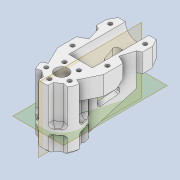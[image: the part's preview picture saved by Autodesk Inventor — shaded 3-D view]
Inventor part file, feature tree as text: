
AUTODESK INVENTOR PART (.ipt)
format: ipt  version: 2020 (Build 240168000, 168)  size: 950,784 bytes
history: native  units: mm
features: projected_geometry x29, sketch x20, extrude x17, thicken_offset x11, fillet x4, chamfer x4, other x4, plane x2, revolve x2, pattern_circular x2, mirror x2, reference x2, hole x1
ambient origin geometry x8: Origin, YZ Plane, XZ Plane, XY Plane, X Axis, Y Axis, Z Axis, Center Point
bodies: Solid1 (feature_tree)
feature tree (100):
  extrude  "Extrusion1"  Depth=12.0mm
  extrude  "Extrusion2"  Depth=18.0mm
  extrude  "Extrusion3"  Depth=20.0mm
  extrude  "Extrusion4"  Depth=60.0mm TaperAngle=0.0deg
  extrude  "Extrusion5"  Depth=45.0mm TaperAngle=0.0deg
  plane  "Work Plane1"
  revolve  "Revolution1"  [1 undecoded]
  extrude  "Extrusion6"  Depth=45.0mm TaperAngle=0.0deg
  pattern_circular  "Circular Pattern1"  Count=9  [1 undecoded]
  thicken_offset  "Thicken1"
  extrude  "Extrusion7"  Depth=2.0mm
  extrude  "Extrusion8"  Depth=90.0mm TaperAngle=0.0deg
  extrude  "Extrusion9"  Depth=50.0mm
  thicken_offset  "Thicken2"
  thicken_offset  "Thicken3"
  extrude  "Extrusion10"  Depth=4.2mm
  extrude  "Extrusion11"  Depth=125.0mm
  mirror  "Mirror1"
  thicken_offset  "Thicken4"
  thicken_offset  "Thicken5"
  revolve  "Revolution2"  [1 undecoded]
  fillet  "Fillet1"  Radius=2.0mm
  thicken_offset  "Thicken6"
  thicken_offset  "Thicken7"
  extrude  "Extrusion12"  Depth=2.0mm
  extrude  "Extrusion13"  Depth=2.0mm
  pattern_circular  "Circular Pattern2"  Count=4  [1 undecoded]
  extrude  "Extrusion14"  Depth=2.0mm
  extrude  "Extrusion15"  Depth=2.0mm
  extrude  "Extrusion16"  Depth=2.0mm TaperAngle=0.0deg
  mirror  "Mirror2"
  plane  "Work Plane2"
  extrude  "Extrusion17"  Depth=2.0mm
  chamfer  "Chamfer1"  Angle=30.0deg  [1 undecoded]
  hole  "Hole1"  [1 undecoded]
  chamfer  "Chamfer2"  Distance=4.2mm
  chamfer  "Chamfer3"  Angle=30.0deg  [1 undecoded]
  fillet  "Fillet3"  Radius=60.0mm
  fillet  "Fillet4"  Radius=4.0mm
  chamfer  "Chamfer5"  Distance=2.0mm
  fillet  "Fillet5"  Radius=2.0mm
  thicken_offset  "Thicken8"
  thicken_offset  "Thicken9"
  thicken_offset  "Thicken10"
  thicken_offset  "Thicken11"
  sketch  "Sketch1"  dims[d0=12.0mm d1=12.0mm]
  reference  "Reference1"
  sketch  "Sketch2"  dims[d2=18.0mm d3=18.0mm]
  projected_geometry  "Projected Loop1"
  sketch  "Sketch3"  dims[d4=60.0mm d5=0.0mm d6=20.0mm]
  projected_geometry  "Projected Loop2"
  sketch  "Sketch4"  dims[d7=40.0mm d8=60.0mm d9=0.0mm]
  projected_geometry  "Projected Loop3"
  projected_geometry  "Projected Loop4"
  sketch  "Sketch5"  dims[d10=40.0mm d11=45.0mm d12=0.0mm]
  projected_geometry  "Projected Loop5"
  projected_geometry  "Projected Loop6"
  sketch  "Sketch6"  dims[d13=45.0mm d14=0.0mm d15=8.0mm]
  projected_geometry  "Projected Loop7"
  projected_geometry  "Projected Loop8"
  projected_geometry  "Projected Loop9"
  sketch  "Sketch7"  dims[d16=8.0mm d17=45.0mm d18=0.0mm]
  projected_geometry  "Projected Loop10"
  sketch  "Sketch8"  dims[d19=7.0mm]
  projected_geometry  "Projected Loop11"
  sketch  "Sketch9"  dims[d20=35.0mm]
  projected_geometry  "Projected Loop12"
  sketch  "Sketch10"  dims[d21=45.0mm]
  projected_geometry  "Projected Loop13"
  projected_geometry  "Projected Loop14"
  projected_geometry  "Projected Loop15"
  projected_geometry  "Projected Loop16"
  projected_geometry  "Projected Loop17"
  sketch  "Sketch11"  dims[d22=90.0deg]
  projected_geometry  "Projected Loop18"
  sketch  "Sketch12"  dims[d23=13.0mm]
  projected_geometry  "Projected Loop19"
  sketch  "Sketch13"  dims[d24=4.2mm d25=90.0mm d26=0.0mm]
  projected_geometry  "Projected Loop20"
  projected_geometry  "Projected Loop21"
  sketch  "Sketch14"  dims[d27=50.0mm d28=360.0deg d30=2.0mm d31=4.0mm]
  projected_geometry  "Projected Loop22"
  sketch  "Sketch15"  dims[d32=14.0mm d33=90.0mm d34=0.0mm]
  projected_geometry  "Projected Loop23"
  sketch  "Sketch16"  dims[d35=50.0mm d36=50.0mm]
  projected_geometry  "Projected Loop24"
  projected_geometry  "Projected Loop25"
  sketch  "Sketch17"  dims[d37=4.2mm d38=4.2mm]
  projected_geometry  "Projected Loop26"
  sketch  "Sketch18"  dims[d39=90.0mm d40=0.0mm d41=125.0mm]
  projected_geometry  "Projected Loop27"
  sketch  "Sketch19"  dims[d42=90.0mm d43=0.0mm d44=2.0mm d45=2.0mm]
  projected_geometry  "Projected Loop28"
  sketch  "Sketch20"  dims[d46=2.0mm d47=2.0mm d48=40.0mm d49=40.0mm d50=4.2mm d51=4.2mm d52=90.0mm d53=0.0mm d54=4.2mm d56=30.0deg d57=60.0mm d59=360.0deg d61=4.2mm d62=30.0deg d63=60.0mm d65=360.0deg d67=4.0mm d68=0.0mm d69=2.0mm d70=2.0mm d71=2.0mm d72=2.0mm d73=12.0mm d74=8.0mm d75=20.0mm d76=90.0deg d77=2.0mm d78=2.0mm d79=2.0mm d80=2.0mm d81=2.0mm d82=15.0mm d83=8.0mm d84=8.0mm d85=4.0mm d86=2.0mm d87=20.0mm d88=0.0mm d89=4.0mm d90=4.0mm d91=4.0mm d92=22.68928mm d93=22.68928mm d94=20.0mm d95=0.0mm d96=40.0mm d97=37.699112mm d99=20.0mm d100=0.0mm d101=20.0mm d102=0.0mm d103=22.68928mm d104=15.0mm d105=17.453293mm d106=20.0mm d107=0.0mm d108=40.0mm d109=5.0mm d110=0.0mm d111=6.0mm d112=2.0mm d113=45.0deg d114=4.2mm d115=6.0mm d116=4.0mm d117=2.0mm d118=90.0deg d119=5.0mm d120=0.0mm d121=4.5mm d122=2.0mm d123=60.0deg d124=4.5mm d125=2.0mm d126=60.0deg d128=2.0mm d129=4.0mm d130=4.0mm d134=3.0mm d135=2.0mm d136=60.0deg d137=2.0mm d138=1.0mm d139=1.0mm d140=1.0mm d141=1.0mm d142=1.0mm d143=1.0mm d144=1.0mm d145=1.0mm]
  projected_geometry  "Projected Loop29"
  reference  "Reference2"
  parser-record x1  (decoder bookkeeping rows leaked as tree rows — omitted from the tree; the rows remain in map.json)
  other  "sub_leg_1.iam"
  other  "carbon_fiber_25_21_300:1"
  other  "joint_connector_6:1"
note: 7 required parameter values undecoded (feature->parameter linkage not recoverable at this tier; creation-order binding heuristic only, values carry confidence <= 0.55)
note: 1 file-system path scrubbed to <path> (originals preserved in map.json)